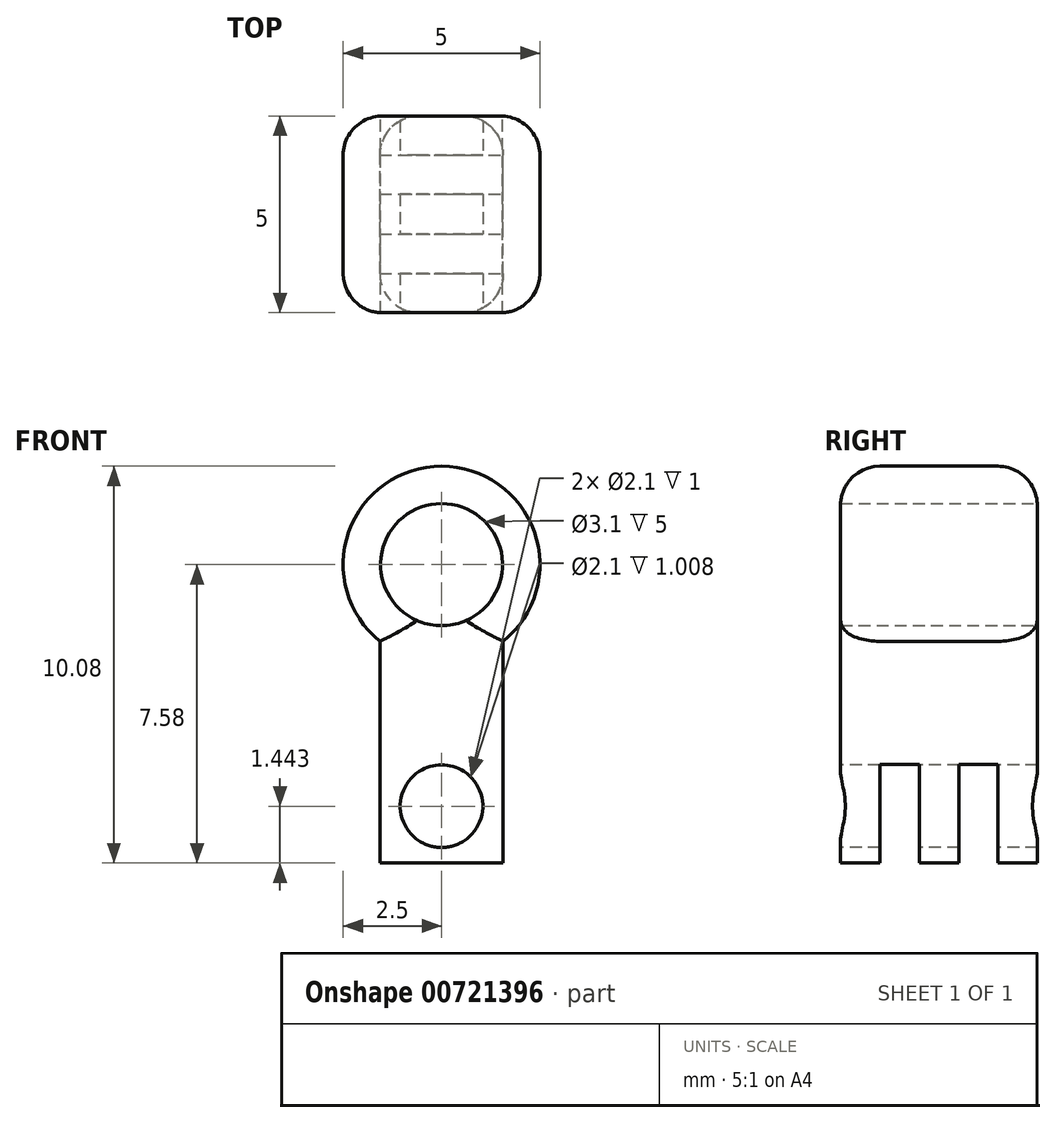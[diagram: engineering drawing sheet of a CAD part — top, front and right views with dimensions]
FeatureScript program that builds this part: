
annotation { "Feature Type Name" : "Feature", "Feature Type Description" : "" }
export const myFeature = defineFeature(function(context is Context, id is Id, definition is map)
    precondition{}
    {
        {
            var Q0;
            Q0=qCreatedBy(makeId("Front.planeOp"),FACE);
            var sketch = newSketch(context, id + "F0", { "sketchPlane" : qUnion([Q0])});
            skCircle(sketch, "E0", {"center": v(0, 0) * mm, "radius": 2.5 * mm});
            skPoint(sketch, "E1.middle", {"position": v(0, -2.5) * mm});
            skLineSegment(sketch, "E2.bottom", {"start": v(-1.57, -7.58) * mm, "end": v(1.57, -7.58) * mm});
            skLineSegment(sketch, "E3", {"start": v(-1.57, -7.58) * mm, "end": v(-1.57, -1.7) * mm});
            skLineSegment(sketch, "E4", {"start": v(-1.57, -1.7) * mm, "end": v(1.57, -1.7) * mm});
            skLineSegment(sketch, "E5", {"start": v(1.57, -1.7) * mm, "end": v(1.57, -7.58) * mm});
            skCircle(sketch, "E6", {"center": v(0, 0) * mm, "radius": 1.55 * mm});
            skSolve(sketch);
        }
        {
            var Q0;
            {var subQ5=sQuery(id+"F0.wireOp",EDGE,"E4");Q0=makeQuery(id+"F0.imprint","IMPRINT",FACE,{"disambiguationData":[TD([[makeQuery(id+"F0.imprint","IMPRINT",EDGE,{"derivedFrom":subQ5}),1.0]])]});}
            var Q1;
            {var subQ5=sQuery(id+"F0.wireOp",EDGE,"E4");Q1=makeQuery(id+"F0.imprint","IMPRINT",FACE,{"disambiguationData":[TD([[makeQuery(id+"F0.imprint","IMPRINT",EDGE,{"derivedFrom":subQ5}),-1.0]])]});}
            extrude(context, id + "F1", {"entities" : qUnion([Q0, Q1]), "endBound" : BoundingType.SYMMETRIC, "depth" : 5 * mm, "offsetDistance" : 25 * mm});
        }
        {
            var Q0;
            {var subQ5=sQuery(id+"F0.wireOp",EDGE,"E2.bottom");Q0=makeQuery(id+"F0.imprint","IMPRINT",FACE,{"disambiguationData":[TD([[makeQuery(id+"F0.imprint","IMPRINT",EDGE,{"derivedFrom":subQ5}),1.0]])]});}
            extrude(context, id + "F2", {"entities" : qUnion([Q0]), "operationType" : NewBodyOperationType.ADD, "endBound" : BoundingType.SYMMETRIC, "depth" : 5 * mm, "offsetDistance" : 25 * mm});
        }
        {
            var Q0;
            Q0=makeQuery(id+"F2.opExtrude","CAP_EDGE",EDGE,{"disambiguationData":[OSD([sQuery(id+"F0.wireOp",EDGE,"E3")])],"isStart":false});
            var Q1;
            Q1=makeQuery(id+"F1.opExtrude","CAP_EDGE",EDGE,{"disambiguationData":[OSD([sQuery(id+"F0.wireOp",EDGE,"E0")])],"isStart":false});
            var Q2;
            Q2=makeQuery(id+"F2.opExtrude","CAP_EDGE",EDGE,{"disambiguationData":[OSD([sQuery(id+"F0.wireOp",EDGE,"E5")])],"isStart":false});
            var Q3;
            Q3=makeQuery(id+"F1.opExtrude","CAP_EDGE",EDGE,{"disambiguationData":[OSD([sQuery(id+"F0.wireOp",EDGE,"E0")])],"isStart":true});
            var Q4;
            Q4=makeQuery(id+"F2.opExtrude","CAP_EDGE",EDGE,{"disambiguationData":[OSD([sQuery(id+"F0.wireOp",EDGE,"E3")])],"isStart":true});
            var Q5;
            Q5=makeQuery(id+"F2.opExtrude","CAP_EDGE",EDGE,{"disambiguationData":[OSD([sQuery(id+"F0.wireOp",EDGE,"E5")])],"isStart":true});
            fillet(context, id + "F3", {"entities" : qUnion([Q0, Q1, Q2, Q3, Q4, Q5]), "radius" : 1 * mm, "tangentPropagation" : true, "allowEdgeOverflow" : false});
        }
        {
            var Q0;
            Q0=makeQuery(id+"F2.opExtrude","SWEPT_FACE",FACE,{"disambiguationData":[OSD([sQuery(id+"F0.wireOp",EDGE,"E5")])]});
            var sketch = newSketch(context, id + "F4", { "sketchPlane" : qUnion([Q0])});
            skSolve(sketch);
        }
        {
            var Q0;
            {var subQ0=sQuery(id+"F0.wireOp",EDGE,"E5");Q0=makeQuery(id+"F4.imprint","IMPRINT",FACE,{"disambiguationData":[TD([[makeQuery(id+"F4.imprint","IMPRINT",EDGE,{"derivedFrom":makeQuery(id+"F2.opExtrude","SWEPT_EDGE",EDGE,{"disambiguationData":[OSD([sQuery(id+"F0.wireOp",EDGE,"E2.bottom"),subQ0])]})}),1.0]])]});}
            var sketch = newSketch(context, id + "F5", { "sketchPlane" : qUnion([Q0])});
            skLineSegment(sketch, "E7", {"start": v(-2.5, -3.2) * mm, "end": v(2.5, -3.2) * mm});
            skLineSegment(sketch, "E8.bottom", {"start": v(-1.5, -7.58) * mm, "end": v(-0.5, -7.58) * mm});
            skLineSegment(sketch, "E8.top", {"start": v(-1.5, -5.07) * mm, "end": v(-0.5, -5.07) * mm});
            skLineSegment(sketch, "E8.left", {"start": v(-1.5, -7.58) * mm, "end": v(-1.5, -5.07) * mm});
            skLineSegment(sketch, "E8.right", {"start": v(-0.5, -7.58) * mm, "end": v(-0.5, -5.07) * mm});
            skLineSegment(sketch, "E9.bottom", {"start": v(0.51, -7.58) * mm, "end": v(1.52, -7.58) * mm});
            skLineSegment(sketch, "E9.top", {"start": v(0.51, -5.07) * mm, "end": v(1.52, -5.07) * mm});
            skLineSegment(sketch, "E9.left", {"start": v(0.51, -7.58) * mm, "end": v(0.51, -5.07) * mm});
            skLineSegment(sketch, "E9.right", {"start": v(1.52, -7.58) * mm, "end": v(1.52, -5.07) * mm});
            skSolve(sketch);
        }
        {
            var Q0;
            {var subQ0=sQuery(id+"F5.wireOp",EDGE,"E8.right");var subQ1=sQuery(id+"F5.wireOp",EDGE,"E8.top");var subQ2=makeQuery(id+"F5.imprint","INTERSECT",VERTEX,{"derivedFrom":[subQ1,subQ0]});Q0=makeQuery(id+"F5.imprint","IMPRINT",FACE,{"disambiguationData":[TD([[makeQuery(id+"F5.imprint","IMPRINT",EDGE,{"disambiguationData":[TD([[subQ2,1.0]])],"derivedFrom":subQ1}),-1.0]])]});}
            var Q1;
            {var subQ0=sQuery(id+"F5.wireOp",EDGE,"E9.left");var subQ1=sQuery(id+"F5.wireOp",EDGE,"E9.top");var subQ2=makeQuery(id+"F5.imprint","INTERSECT",VERTEX,{"derivedFrom":[subQ1,subQ0]});Q1=makeQuery(id+"F5.imprint","IMPRINT",FACE,{"disambiguationData":[TD([[makeQuery(id+"F5.imprint","IMPRINT",EDGE,{"disambiguationData":[TD([[subQ2,-1.0]])],"derivedFrom":subQ1}),-1.0]])]});}
            extrude(context, id + "F6", {"entities" : qUnion([Q0, Q1]), "operationType" : NewBodyOperationType.REMOVE, "oppositeDirection" : true, "depth" : 25 * mm, "offsetDistance" : 25 * mm});
        }
        {
            var Q0;
            {var subQ0=sQuery(id+"F0.wireOp",EDGE,"E0");Q0=makeQuery(id+"F2.boolean.opBoolean","MERGE",FACE,{"derivedFrom":[makeQuery(id+"F1.opExtrude","CAP_FACE",FACE,{"disambiguationData":[OSD([subQ0,sQuery(id+"F0.wireOp",EDGE,"E6")])],"isStart":false}),makeQuery(id+"F2.opExtrude","CAP_FACE",FACE,{"disambiguationData":[OSD([subQ0,sQuery(id+"F0.wireOp",EDGE,"E2.bottom"),sQuery(id+"F0.wireOp",EDGE,"E3"),sQuery(id+"F0.wireOp",EDGE,"E5")])],"isStart":false})]});}
            var sketch = newSketch(context, id + "F7", { "sketchPlane" : qUnion([Q0])});
            skCircle(sketch, "E10", {"center": v(0, -6.14) * mm, "radius": 1.05 * mm});
            skSolve(sketch);
        }
        {
            var Q0;
            Q0 = qSketchRegion(id + "F7", true);
            extrude(context, id + "F8", {"entities" : qUnion([Q0]), "operationType" : NewBodyOperationType.REMOVE, "oppositeDirection" : true, "depth" : 25 * mm, "offsetDistance" : 25 * mm});
        }
    });
